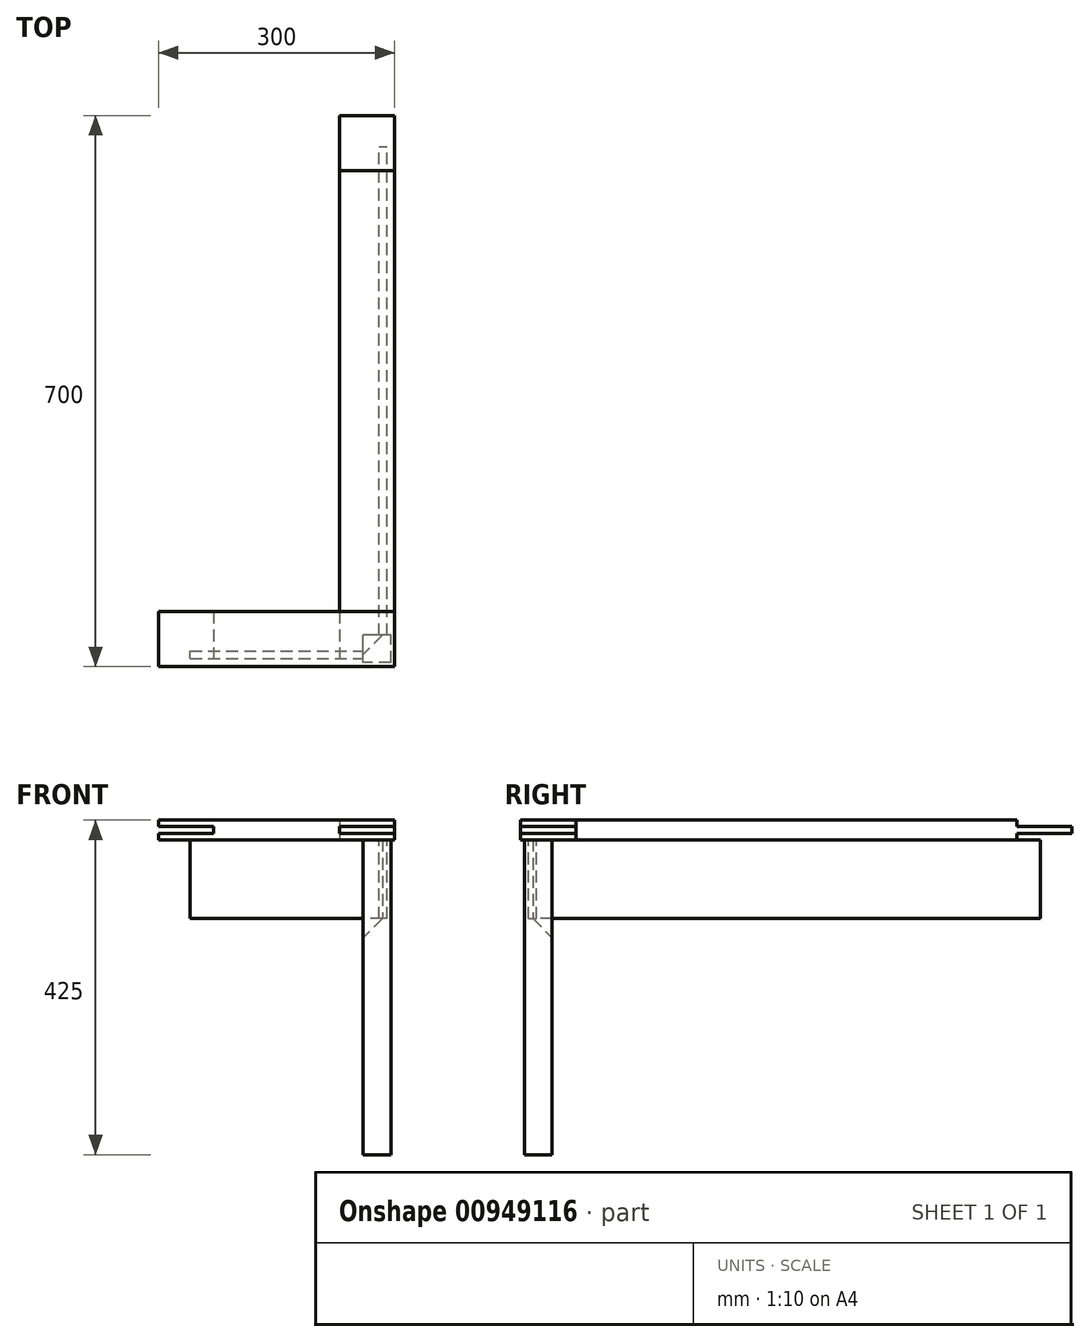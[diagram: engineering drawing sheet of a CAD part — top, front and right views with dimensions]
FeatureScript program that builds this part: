
annotation { "Feature Type Name" : "Feature", "Feature Type Description" : "" }
export const myFeature = defineFeature(function(context is Context, id is Id, definition is map)
    precondition{}
    {
        {
            var Q0;
            Q0=qCreatedBy(makeId("Top.planeOp"),FACE);
            var sketch = newSketch(context, id + "F0", { "sketchPlane" : qUnion([Q0])});
            skLineSegment(sketch, "E0.bottom", {"start": v(0, 0) * mm, "end": v(70, 0) * mm});
            skLineSegment(sketch, "E0.top", {"start": v(0, -700) * mm, "end": v(70, -700) * mm});
            skLineSegment(sketch, "E0.left", {"start": v(0, 0) * mm, "end": v(0, -700) * mm});
            skLineSegment(sketch, "E0.right", {"start": v(70, 0) * mm, "end": v(70, -700) * mm});
            skLineSegment(sketch, "E1.bottom", {"start": v(70, 0) * mm, "end": v(-230, 0) * mm});
            skLineSegment(sketch, "E1.top", {"start": v(70, -70) * mm, "end": v(-230, -70) * mm});
            skLineSegment(sketch, "E1.left", {"start": v(70, 0) * mm, "end": v(70, -70) * mm});
            skLineSegment(sketch, "E1.right", {"start": v(-230, 0) * mm, "end": v(-230, -70) * mm});
            skLineSegment(sketch, "E2.bottom", {"start": v(-230, 0) * mm, "end": v(-160, 0) * mm});
            skLineSegment(sketch, "E2.top", {"start": v(-230, -700) * mm, "end": v(-160, -700) * mm});
            skLineSegment(sketch, "E2.left", {"start": v(-230, 0) * mm, "end": v(-230, -700) * mm});
            skLineSegment(sketch, "E2.right", {"start": v(-160, 0) * mm, "end": v(-160, -700) * mm});
            skLineSegment(sketch, "E3.bottom", {"start": v(-230, -700) * mm, "end": v(70, -700) * mm});
            skLineSegment(sketch, "E3.top", {"start": v(-230, -630) * mm, "end": v(70, -630) * mm});
            skLineSegment(sketch, "E3.left", {"start": v(-230, -700) * mm, "end": v(-230, -630) * mm});
            skLineSegment(sketch, "E3.right", {"start": v(70, -700) * mm, "end": v(70, -630) * mm});
            skPoint(sketch, "E4", {"position": v(-80, -630) * mm});
            skPoint(sketch, "E5", {"position": v(-160, -350) * mm});
            skSolve(sketch);
        }
        {
            var Q0;
            {var subQ0=sQuery(id+"F0.wireOp",EDGE,"E0.top");Q0=makeQuery(id+"F0.imprint","IMPRINT",FACE,{"disambiguationData":[TD([[makeQuery(id+"F0.imprint","IMPRINT",EDGE,{"derivedFrom":subQ0}),1.0]])]});}
            var Q1;
            {var subQ0=sQuery(id+"F0.wireOp",EDGE,"E1.top");var subQ1=sQuery(id+"F0.wireOp",EDGE,"E0.left");var subQ2=makeQuery(id+"F0.imprint","INTERSECT",VERTEX,{"derivedFrom":[subQ1,subQ0]});Q1=makeQuery(id+"F0.imprint","IMPRINT",FACE,{"disambiguationData":[TD([[makeQuery(id+"F0.imprint","IMPRINT",EDGE,{"disambiguationData":[TD([[subQ2,-1.0]])],"derivedFrom":subQ1}),1.0]])]});}
            var Q2;
            {var subQ0=sQuery(id+"F0.wireOp",EDGE,"E0.bottom");Q2=makeQuery(id+"F0.imprint","IMPRINT",FACE,{"disambiguationData":[TD([[makeQuery(id+"F0.imprint","IMPRINT",EDGE,{"derivedFrom":subQ0}),-1.0]])]});}
            extrude(context, id + "F1", {"entities" : qUnion([Q0, Q1, Q2]), "oppositeDirection" : true, "depth" : 25 * mm, "offsetDistance" : 25 * mm});
        }
        {
            var Q0;
            Q0=makeQuery(id+"F1.opExtrude","SWEPT_FACE",FACE,{"disambiguationData":[OSD([sQuery(id+"F0.wireOp",EDGE,"E0.right")])]});
            var sketch = newSketch(context, id + "F2", { "sketchPlane" : qUnion([Q0])});
            skLineSegment(sketch, "E6.bottom", {"start": v(0, 0) * mm, "end": v(-70, 0) * mm});
            skLineSegment(sketch, "E6.top", {"start": v(0, -8) * mm, "end": v(-70, -8) * mm});
            skLineSegment(sketch, "E6.left", {"start": v(0, 0) * mm, "end": v(0, -8) * mm});
            skLineSegment(sketch, "E6.right", {"start": v(-70, 0) * mm, "end": v(-70, -8) * mm});
            skLineSegment(sketch, "E7.bottom", {"start": v(0, -25) * mm, "end": v(-70, -25) * mm});
            skLineSegment(sketch, "E7.top", {"start": v(0, -17) * mm, "end": v(-70, -17) * mm});
            skLineSegment(sketch, "E7.left", {"start": v(0, -25) * mm, "end": v(0, -17) * mm});
            skLineSegment(sketch, "E7.right", {"start": v(-70, -25) * mm, "end": v(-70, -17) * mm});
            skLineSegment(sketch, "E8.bottom", {"start": v(-700, 0) * mm, "end": v(-630, 0) * mm});
            skLineSegment(sketch, "E8.top", {"start": v(-700, -8) * mm, "end": v(-630, -8) * mm});
            skLineSegment(sketch, "E8.left", {"start": v(-700, 0) * mm, "end": v(-700, -8) * mm});
            skLineSegment(sketch, "E8.right", {"start": v(-630, 0) * mm, "end": v(-630, -8) * mm});
            skLineSegment(sketch, "E9.bottom", {"start": v(-700, -25) * mm, "end": v(-630, -25) * mm});
            skLineSegment(sketch, "E9.top", {"start": v(-700, -17) * mm, "end": v(-630, -17) * mm});
            skLineSegment(sketch, "E9.left", {"start": v(-700, -25) * mm, "end": v(-700, -17) * mm});
            skLineSegment(sketch, "E9.right", {"start": v(-630, -25) * mm, "end": v(-630, -17) * mm});
            skSolve(sketch);
        }
        {
            var Q0;
            Q0 = qSketchRegion(id + "F2", true);
            var Q1;
            Q1=makeQuery(id+"F1.opExtrude","SWEPT_FACE",FACE,{"disambiguationData":[OSD([sQuery(id+"F0.wireOp",EDGE,"E0.left")])]});
            extrude(context, id + "F3", {"entities" : qUnion([Q0]), "operationType" : NewBodyOperationType.REMOVE, "endBound" : BoundingType.UP_TO_SURFACE, "oppositeDirection" : true, "depth" : 25 * mm, "endBoundEntityFace" : qUnion([Q1]), "offsetDistance" : 25 * mm});
        }
        {
            var Q0;
            {var subQ0=sQuery(id+"F0.wireOp",EDGE,"E0.top");Q0=makeQuery(id+"F0.imprint","IMPRINT",FACE,{"disambiguationData":[TD([[makeQuery(id+"F0.imprint","IMPRINT",EDGE,{"derivedFrom":subQ0}),1.0]])]});}
            var Q1;
            {var subQ0=sQuery(id+"F0.wireOp",EDGE,"E3.bottom");Q1=makeQuery(id+"F0.imprint","IMPRINT",FACE,{"disambiguationData":[TD([[makeQuery(id+"F0.imprint","IMPRINT",EDGE,{"derivedFrom":subQ0}),1.0]])]});}
            var Q2;
            {var subQ0=sQuery(id+"F0.wireOp",EDGE,"E2.top");Q2=makeQuery(id+"F0.imprint","IMPRINT",FACE,{"disambiguationData":[TD([[makeQuery(id+"F0.imprint","IMPRINT",EDGE,{"derivedFrom":subQ0}),1.0]])]});}
            var Q3;
            Q3=makeQuery(id+"F1.opExtrude","CAP_FACE",FACE,{"disambiguationData":[OSD([sQuery(id+"F0.wireOp",EDGE,"E0.bottom"),sQuery(id+"F0.wireOp",EDGE,"E0.top"),sQuery(id+"F0.wireOp",EDGE,"E0.left"),sQuery(id+"F0.wireOp",EDGE,"E0.right")])],"isStart":false});
            extrude(context, id + "F4", {"entities" : qUnion([Q0, Q1, Q2]), "endBound" : BoundingType.UP_TO_SURFACE, "oppositeDirection" : true, "depth" : 25 * mm, "endBoundEntityFace" : qUnion([Q3]), "offsetDistance" : 25 * mm});
        }
        {
            var Q0;
            Q0=makeQuery(id+"F4.opExtrude","SWEPT_FACE",FACE,{"disambiguationData":[OSD([sQuery(id+"F0.wireOp",EDGE,"E0.top"),sQuery(id+"F0.wireOp",EDGE,"E2.top"),sQuery(id+"F0.wireOp",EDGE,"E3.bottom")])]});
            var sketch = newSketch(context, id + "F5", { "sketchPlane" : qUnion([Q0])});
            skLineSegment(sketch, "E10.bottom", {"start": v(70, -8) * mm, "end": v(0, -8) * mm});
            skLineSegment(sketch, "E10.top", {"start": v(70, -17) * mm, "end": v(0, -17) * mm});
            skLineSegment(sketch, "E10.left", {"start": v(70, -8) * mm, "end": v(70, -17) * mm});
            skLineSegment(sketch, "E10.right", {"start": v(0, -8) * mm, "end": v(0, -17) * mm});
            skLineSegment(sketch, "E11.bottom", {"start": v(-230, -8) * mm, "end": v(-160, -8) * mm});
            skLineSegment(sketch, "E11.top", {"start": v(-230, -17) * mm, "end": v(-160, -17) * mm});
            skLineSegment(sketch, "E11.left", {"start": v(-230, -8) * mm, "end": v(-230, -17) * mm});
            skLineSegment(sketch, "E11.right", {"start": v(-160, -8) * mm, "end": v(-160, -17) * mm});
            skSolve(sketch);
        }
        {
            var Q0;
            Q0 = qSketchRegion(id + "F5", true);
            var Q1;
            Q1=makeQuery(id+"F4.opExtrude","SWEPT_FACE",FACE,{"disambiguationData":[OSD([sQuery(id+"F0.wireOp",EDGE,"E3.top")])]});
            extrude(context, id + "F6", {"entities" : qUnion([Q0]), "operationType" : NewBodyOperationType.REMOVE, "endBound" : BoundingType.UP_TO_SURFACE, "oppositeDirection" : true, "depth" : 25 * mm, "endBoundEntityFace" : qUnion([Q1]), "offsetDistance" : 25 * mm});
        }
        {
            var Q0;
            Q0=sQuery(id+"F0.wireOp",EDGE,"E3.top");
            cPoint(context, id + "F7", {"entities" : qUnion([Q0]), "parameter" : 0.5});
        }
        {
            var Q0;
            Q0=makeQuery(id+"F1.opExtrude","SWEPT_FACE",FACE,{"disambiguationData":[OSD([sQuery(id+"F0.wireOp",EDGE,"E0.right")])]});
            var Q1;
            Q1 = qCreatedBy(id + "F7" ,VERTEX);
            cPlane(context, id + "F8", {"entities" : qUnion([Q0, Q1]), "cplaneType" : CPlaneType.PLANE_POINT, "offset" : 25 * mm, "width" : 150 * mm, "height" : 150 * mm});
        }
        {
            var Q0;
            Q0=sQuery(id+"F0.wireOp",EDGE,"E2.right");
            cPoint(context, id + "F9", {"entities" : qUnion([Q0]), "parameter" : 0.5});
        }
        {
            var Q0;
            Q0=makeQuery(id+"F4.opExtrude","SWEPT_FACE",FACE,{"disambiguationData":[OSD([sQuery(id+"F0.wireOp",EDGE,"E0.top"),sQuery(id+"F0.wireOp",EDGE,"E2.top"),sQuery(id+"F0.wireOp",EDGE,"E3.bottom")])]});
            var Q1;
            Q1 = qCreatedBy(id + "F9" ,VERTEX);
            cPlane(context, id + "F10", {"entities" : qUnion([Q0, Q1]), "cplaneType" : CPlaneType.PLANE_POINT, "offset" : 25 * mm, "width" : 150 * mm, "height" : 150 * mm});
        }
        {
            var Q0;
            Q0=makeQuery(id+"F1.opExtrude","CAP_FACE",FACE,{"disambiguationData":[OSD([sQuery(id+"F0.wireOp",EDGE,"E0.bottom"),sQuery(id+"F0.wireOp",EDGE,"E0.top"),sQuery(id+"F0.wireOp",EDGE,"E0.left"),sQuery(id+"F0.wireOp",EDGE,"E0.right")])],"isStart":false});
            var sketch = newSketch(context, id + "F11", { "sketchPlane" : qUnion([Q0])});
            skLineSegment(sketch, "E12.bottom", {"start": v(65, 695) * mm, "end": v(30, 695) * mm});
            skLineSegment(sketch, "E12.top", {"start": v(65, 660) * mm, "end": v(30, 660) * mm});
            skLineSegment(sketch, "E12.left", {"start": v(65, 695) * mm, "end": v(65, 660) * mm});
            skLineSegment(sketch, "E12.right", {"start": v(30, 695) * mm, "end": v(30, 660) * mm});
            skSolve(sketch);
        }
        {
            var Q0;
            Q0 = qSketchRegion(id + "F11", true);
            extrude(context, id + "F12", {"entities" : qUnion([Q0]), "depth" : 400 * mm, "offsetDistance" : 25 * mm});
        }
        {
            var Q0;
            Q0=makeQuery(id+"F12.opExtrude","SWEPT_EDGE",EDGE,{"disambiguationData":[OSD([sQuery(id+"F11.wireOp",EDGE,"E12.top"),sQuery(id+"F11.wireOp",EDGE,"E12.right")])]});
            var Q1;
            Q1=makeQuery(id+"F12.opExtrude","SWEPT_EDGE",EDGE,{"disambiguationData":[OSD([sQuery(id+"F11.wireOp",EDGE,"E12.bottom"),sQuery(id+"F11.wireOp",EDGE,"E12.left")])]});
            cPlane(context, id + "F13", {"entities" : qUnion([Q0, Q1]), "cplaneType" : CPlaneType.LINE_ANGLE, "offset" : 25 * mm, "angle" : 0 * degree, "width" : 150 * mm, "height" : 150 * mm});
        }
        {
            var Q0;
            Q0=qCreatedBy(id+"F13.planeOp",FACE);
            var sketch = newSketch(context, id + "F14", { "sketchPlane" : qUnion([Q0])});
            skLineSegment(sketch, "E13", {"start": v(-487.9, -149.63) * mm, "end": v(-505.15, -125) * mm});
            skLineSegment(sketch, "E14", {"start": v(-505.15, -125) * mm, "end": v(-505.15, -25) * mm});
            skLineSegment(sketch, "E15", {"start": v(-505.15, -25) * mm, "end": v(-487.9, -25) * mm});
            skLineSegment(sketch, "E16", {"start": v(-487.9, -25) * mm, "end": v(-487.9, -149.63) * mm});
            skSolve(sketch);
        }
        {
            var Q0;
            Q0 = qSketchRegion(id + "F14", true);
            extrude(context, id + "F15", {"entities" : qUnion([Q0]), "operationType" : NewBodyOperationType.REMOVE, "endBound" : BoundingType.SYMMETRIC, "depth" : 50 * mm, "offsetDistance" : 25 * mm});
        }
        {
            var Q0;
            Q0=makeQuery(id+"F4.opExtrude","CAP_FACE",FACE,{"disambiguationData":[OSD([sQuery(id+"F0.wireOp",EDGE,"E0.top"),sQuery(id+"F0.wireOp",EDGE,"E0.right"),sQuery(id+"F0.wireOp",EDGE,"E2.top"),sQuery(id+"F0.wireOp",EDGE,"E2.left"),sQuery(id+"F0.wireOp",EDGE,"E3.bottom"),sQuery(id+"F0.wireOp",EDGE,"E3.top")])],"isStart":false});
            var sketch = newSketch(context, id + "F16", { "sketchPlane" : qUnion([Q0])});
            skPoint(sketch, "E17", {"position": v(65, 695) * mm});
            skSolve(sketch);
        }
        {
            var Q0;
            Q0=makeQuery(id+"F16.imprint","IMPRINT",FACE,{"disambiguationData":[TD([[makeQuery(id+"F16.imprint","IMPRINT",EDGE,{"derivedFrom":makeQuery(id+"F4.opExtrude","CAP_EDGE",EDGE,{"disambiguationData":[OSD([sQuery(id+"F0.wireOp",EDGE,"E0.right")])],"isStart":false})}),-1.0]])]});
            var sketch = newSketch(context, id + "F17", { "sketchPlane" : qUnion([Q0])});
            skPoint(sketch, "E18", {"position": v(-225, 695) * mm});
            skSolve(sketch);
        }
        {
            var Q0;
            Q0=makeQuery(id+"F1.opExtrude","CAP_FACE",FACE,{"disambiguationData":[OSD([sQuery(id+"F0.wireOp",EDGE,"E0.bottom"),sQuery(id+"F0.wireOp",EDGE,"E0.top"),sQuery(id+"F0.wireOp",EDGE,"E0.left"),sQuery(id+"F0.wireOp",EDGE,"E0.right")])],"isStart":false});
            var sketch = newSketch(context, id + "F18", { "sketchPlane" : qUnion([Q0])});
            skLineSegment(sketch, "E19.bottom", {"start": v(60, 660) * mm, "end": v(50, 660) * mm});
            skLineSegment(sketch, "E19.top", {"start": v(60, 350) * mm, "end": v(50, 350) * mm, "construction": true});
            skLineSegment(sketch, "E19.left", {"start": v(60, 660) * mm, "end": v(60, 350) * mm});
            skLineSegment(sketch, "E19.right", {"start": v(50, 660) * mm, "end": v(50, 350) * mm});
            skLineSegment(sketch, "E20.MirrorCS", {"start": v(50, 40) * mm, "end": v(50, 350) * mm});
            skLineSegment(sketch, "E21.MirrorCS", {"start": v(60, 40) * mm, "end": v(60, 350) * mm});
            skLineSegment(sketch, "E22", {"start": v(60, 40) * mm, "end": v(50, 40) * mm});
            skSolve(sketch);
        }
        {
            var Q0;
            Q0 = qSketchRegion(id + "F18", true);
            extrude(context, id + "F19", {"entities" : qUnion([Q0]), "depth" : 100 * mm, "offsetDistance" : 25 * mm});
        }
        {
            var Q0;
            Q0=makeQuery(id+"F16.imprint","IMPRINT",FACE,{"disambiguationData":[TD([[makeQuery(id+"F16.imprint","IMPRINT",EDGE,{"derivedFrom":makeQuery(id+"F4.opExtrude","CAP_EDGE",EDGE,{"disambiguationData":[OSD([sQuery(id+"F0.wireOp",EDGE,"E0.right")])],"isStart":false})}),-1.0]])]});
            var sketch = newSketch(context, id + "F20", { "sketchPlane" : qUnion([Q0])});
            skLineSegment(sketch, "E23.bottom", {"start": v(-190, 690) * mm, "end": v(30, 690) * mm});
            skLineSegment(sketch, "E23.left", {"start": v(-190, 690) * mm, "end": v(-190, 680) * mm});
            skLineSegment(sketch, "E23.right", {"start": v(30, 690) * mm, "end": v(30, 680) * mm});
            skPoint(sketch, "E24", {"position": v(-80, 690) * mm});
            skLineSegment(sketch, "E25", {"start": v(-190, 680) * mm, "end": v(-80, 680) * mm});
            skLineSegment(sketch, "E26", {"start": v(30, 680) * mm, "end": v(-80, 680) * mm});
            skSolve(sketch);
        }
        {
            var Q0;
            Q0 = qSketchRegion(id + "F20", true);
            extrude(context, id + "F21", {"entities" : qUnion([Q0]), "depth" : 100 * mm, "offsetDistance" : 25 * mm});
        }
    });
